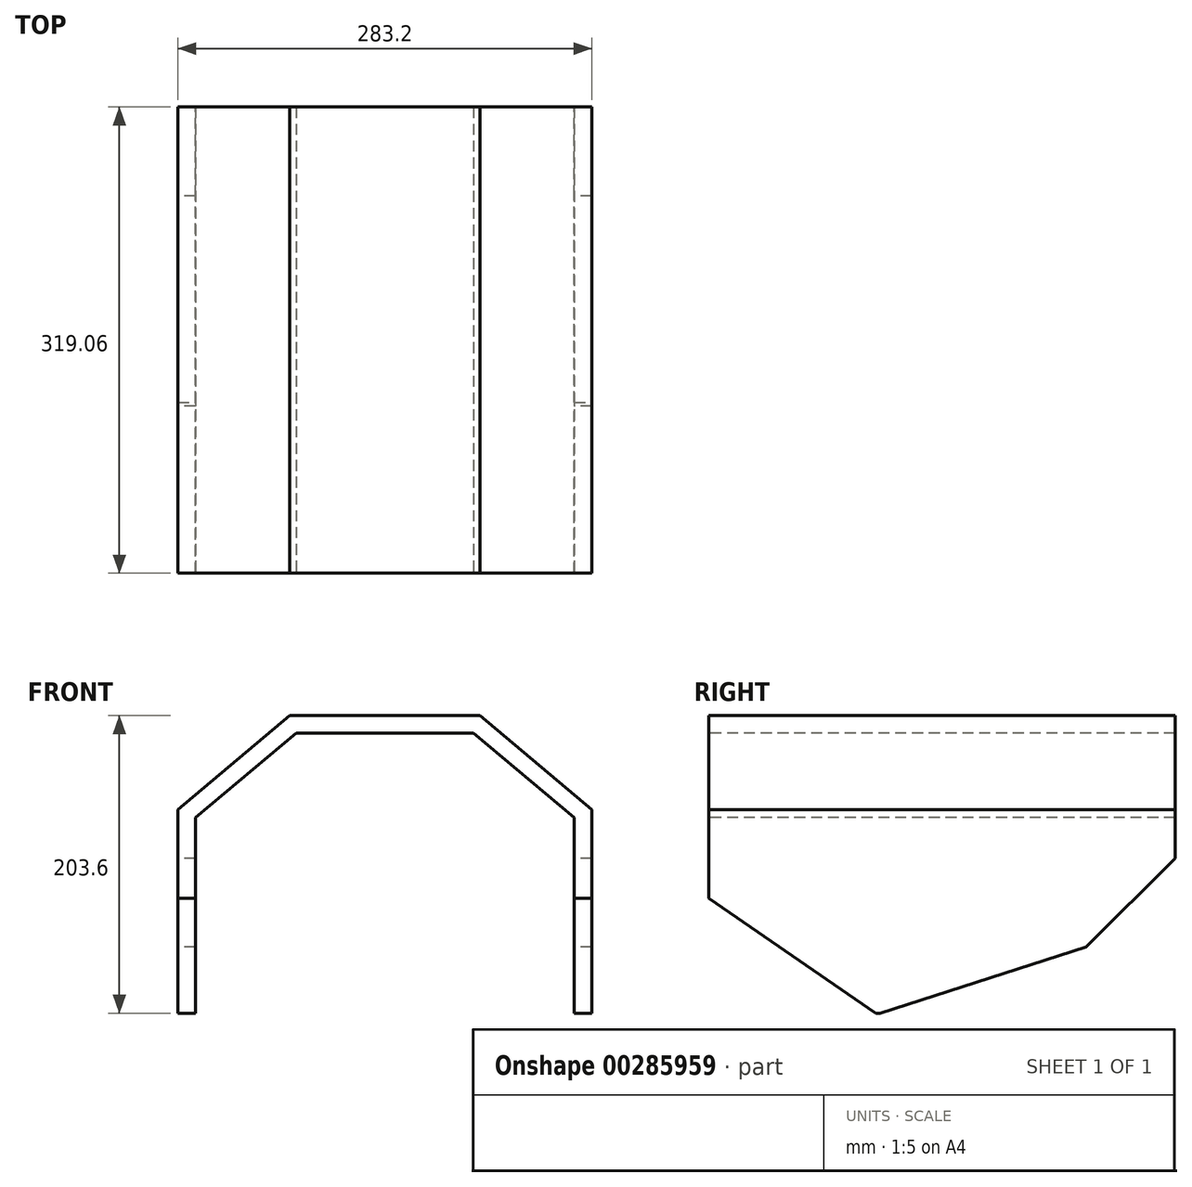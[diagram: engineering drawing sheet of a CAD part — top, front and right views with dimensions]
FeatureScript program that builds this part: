
annotation { "Feature Type Name" : "Feature", "Feature Type Description" : "" }
export const myFeature = defineFeature(function(context is Context, id is Id, definition is map)
    precondition{}
    {
        {
            var Q0;
            Q0=qCreatedBy(makeId("Front.planeOp"),FACE);
            var sketch = newSketch(context, id + "F0", { "sketchPlane" : qUnion([Q0])});
            skLineSegment(sketch, "E0", {"start": v(-65, 101.8) * mm, "end": v(65, 101.8) * mm});
            skLineSegment(sketch, "E1", {"start": v(-60.63, 89.8) * mm, "end": v(60.63, 89.8) * mm});
            skLineSegment(sketch, "E2", {"start": v(65, 101.8) * mm, "end": v(141.6, 37.52) * mm});
            skLineSegment(sketch, "E3", {"start": v(60.63, 89.8) * mm, "end": v(129.6, 31.92) * mm});
            skLineSegment(sketch, "E4", {"start": v(141.6, 37.52) * mm, "end": v(141.6, -101.8) * mm});
            skLineSegment(sketch, "E5", {"start": v(129.6, 31.92) * mm, "end": v(129.6, -101.8) * mm});
            skLineSegment(sketch, "E6", {"start": v(-65, 101.8) * mm, "end": v(-141.6, 37.52) * mm});
            skLineSegment(sketch, "E7", {"start": v(-60.63, 89.8) * mm, "end": v(-129.6, 31.92) * mm});
            skLineSegment(sketch, "E8", {"start": v(-141.6, 37.52) * mm, "end": v(-141.6, -101.8) * mm});
            skLineSegment(sketch, "E9", {"start": v(-129.6, 31.92) * mm, "end": v(-129.6, -101.8) * mm});
            skLineSegment(sketch, "E10", {"start": v(141.6, -101.8) * mm, "end": v(129.6, -101.8) * mm});
            skLineSegment(sketch, "E11", {"start": v(-129.6, -101.8) * mm, "end": v(-141.6, -101.8) * mm});
            skSolve(sketch);
        }
        {
            var Q0;
            Q0=makeQuery(id+"F0.imprint","IMPRINT",FACE,{"disambiguationData":[TD([[makeQuery(id+"F0.imprint","IMPRINT",EDGE,{"derivedFrom":sQuery(id+"F0.wireOp",EDGE,"E0")}),-1.0]])]});
            extrude(context, id + "F1", {"entities" : qUnion([Q0]), "oppositeDirection" : true, "depth" : 320 * mm});
        }
        {
            var Q0;
            Q0=qCreatedBy(makeId("Right.planeOp"),FACE);
            var sketch = newSketch(context, id + "F2", { "sketchPlane" : qUnion([Q0])});
            skLineSegment(sketch, "E12", {"start": v(0.94, -23.12) * mm, "end": v(0.94, 106.3) * mm});
            skLineSegment(sketch, "E13", {"start": v(320.94, 5.16) * mm, "end": v(320.94, 106.3) * mm});
            skLineSegment(sketch, "E14", {"start": v(0.94, -23.12) * mm, "end": v(116.13, -102.38) * mm});
            skLineSegment(sketch, "E15", {"start": v(116.13, -102.38) * mm, "end": v(259.1, -56.67) * mm});
            skLineSegment(sketch, "E16", {"start": v(259.1, -56.67) * mm, "end": v(320.94, 5.16) * mm});
            skLineSegment(sketch, "E17", {"start": v(0.94, 106.3) * mm, "end": v(-50.58, 106.3) * mm});
            skLineSegment(sketch, "E18", {"start": v(-50.58, 106.3) * mm, "end": v(-50.58, -137.24) * mm});
            skLineSegment(sketch, "E19", {"start": v(-50.58, -137.24) * mm, "end": v(364.99, -137.24) * mm});
            skLineSegment(sketch, "E20", {"start": v(364.99, -137.24) * mm, "end": v(364.99, 106.3) * mm});
            skLineSegment(sketch, "E21", {"start": v(364.99, 106.3) * mm, "end": v(320.94, 106.3) * mm});
            skLineSegment(sketch, "E22.0", {"start": v(320, 101.8) * mm, "end": v(0, 101.8) * mm});
            skSolve(sketch);
        }
        {
            var Q0;
            Q0=makeQuery(id+"F2.imprint","IMPRINT",FACE,{"disambiguationData":[TD([[makeQuery(id+"F2.imprint","IMPRINT",EDGE,{"derivedFrom":sQuery(id+"F2.wireOp",EDGE,"E12")}),1.0]])]});
            extrude(context, id + "F3", {"entities" : qUnion([Q0]), "operationType" : NewBodyOperationType.REMOVE, "endBound" : BoundingType.SYMMETRIC, "depth" : 400 * mm});
        }
    });
